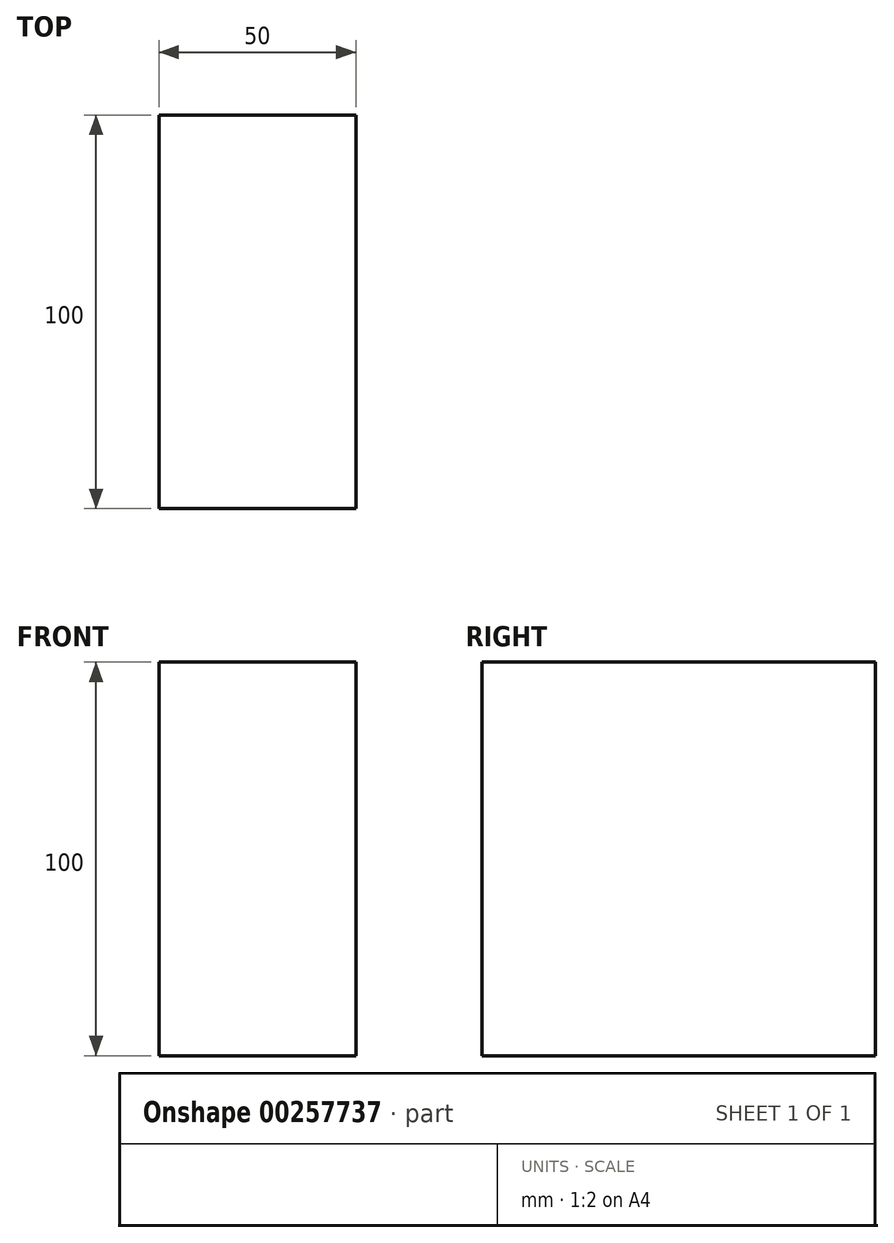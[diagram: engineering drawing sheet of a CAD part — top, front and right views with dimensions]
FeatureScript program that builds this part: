
annotation { "Feature Type Name" : "Feature", "Feature Type Description" : "" }
export const myFeature = defineFeature(function(context is Context, id is Id, definition is map)
    precondition{}
    {
        {
            var Q0;
            Q0=qCreatedBy(makeId("Right.planeOp"),FACE);
            var sketch = newSketch(context, id + "F0", { "sketchPlane" : qUnion([Q0])});
            skLineSegment(sketch, "E0.bottom", {"start": v(0, 0) * mm, "end": v(-100, 0) * mm});
            skLineSegment(sketch, "E0.top", {"start": v(0, 100) * mm, "end": v(-100, 100) * mm});
            skLineSegment(sketch, "E0.left", {"start": v(0, 0) * mm, "end": v(0, 100) * mm});
            skLineSegment(sketch, "E0.right", {"start": v(-100, 0) * mm, "end": v(-100, 100) * mm});
            skSolve(sketch);
        }
        {
            var Q0;
            Q0 = qSketchRegion(id + "F0", true);
            extrude(context, id + "F1", {"entities" : qUnion([Q0]), "depth" : 50 * mm});
        }
    });
